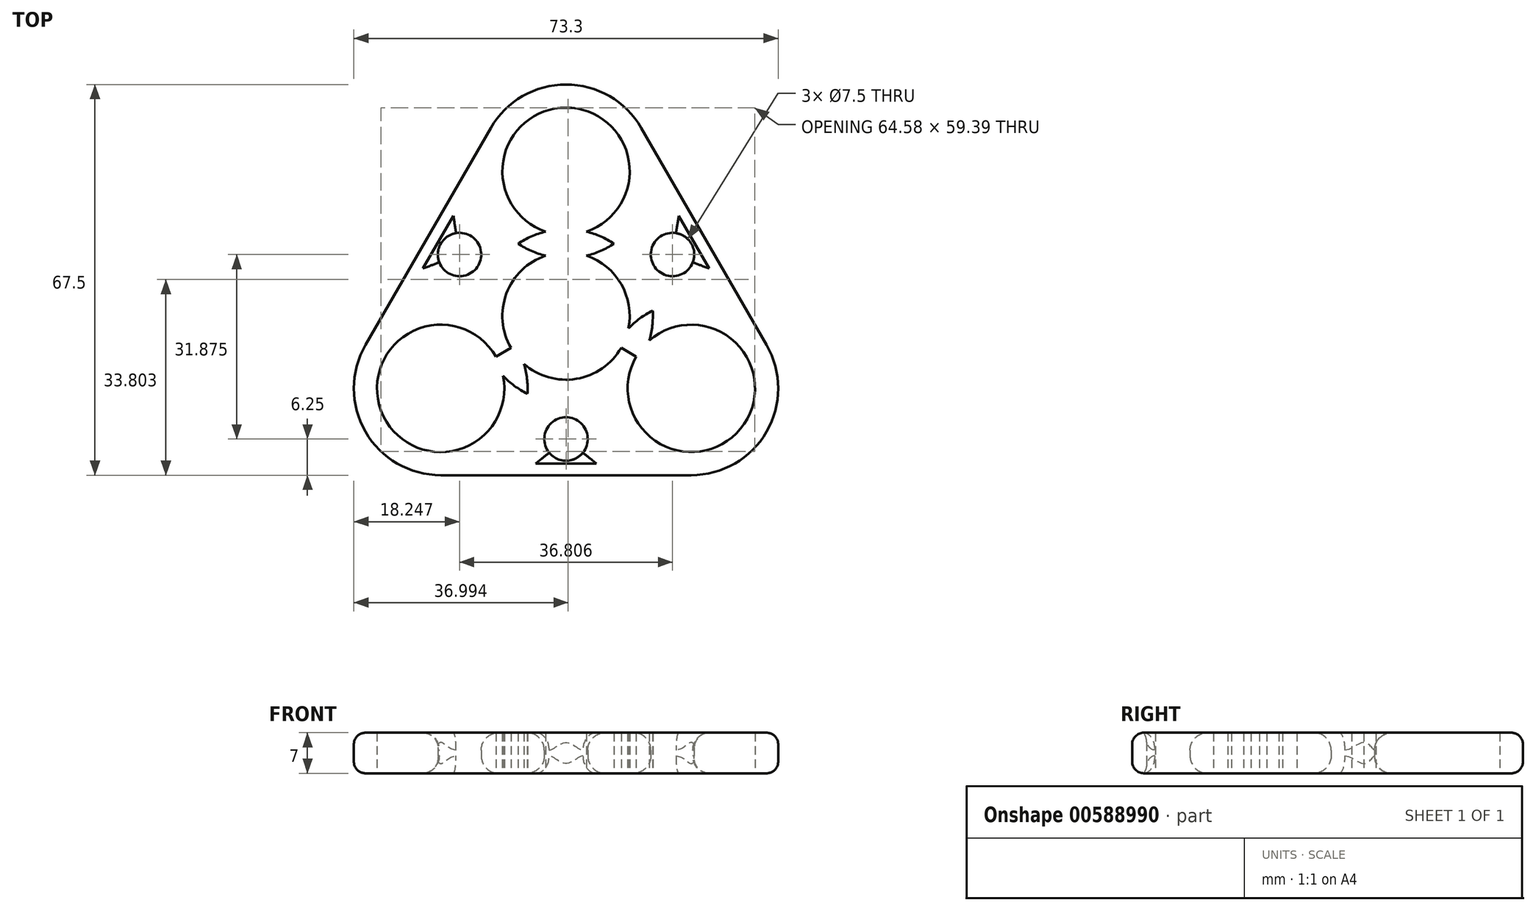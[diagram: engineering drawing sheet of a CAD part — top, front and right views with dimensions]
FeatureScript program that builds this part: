
annotation { "Feature Type Name" : "Feature", "Feature Type Description" : "" }
export const myFeature = defineFeature(function(context is Context, id is Id, definition is map)
    precondition{}
    {
        {
            var Q0;
            Q0=qCreatedBy(makeId("Top.planeOp"),FACE);
            var sketch = newSketch(context, id + "F0", { "sketchPlane" : qUnion([Q0])});
            skCircle(sketch, "E0", {"center": v(0, 0) * mm, "radius": 11 * mm});
            skCircle(sketch, "E1", {"center": v(0, 0) * mm, "radius": 15 * mm});
            skLineSegment(sketch, "E2", {"start": v(0, 0) * mm, "end": v(0, 25) * mm});
            skLineSegment(sketch, "E3", {"start": v(0, 25) * mm, "end": v(0, 0) * mm});
            skLineSegment(sketch, "E4", {"start": v(0, 0) * mm, "end": v(21.65, -12.5) * mm});
            skLineSegment(sketch, "E5", {"start": v(21.65, -12.5) * mm, "end": v(0, 0) * mm});
            skLineSegment(sketch, "E6", {"start": v(0, 0) * mm, "end": v(-21.65, -12.5) * mm});
            skLineSegment(sketch, "E7", {"start": v(-21.65, -12.5) * mm, "end": v(0, 0) * mm});
            skCircle(sketch, "E8", {"center": v(0, 25) * mm, "radius": 11 * mm});
            skCircle(sketch, "E9", {"center": v(21.65, -12.5) * mm, "radius": 11 * mm});
            skCircle(sketch, "E10", {"center": v(21.65, -12.5) * mm, "radius": 15 * mm});
            skCircle(sketch, "E11", {"center": v(0, 25) * mm, "radius": 15 * mm});
            skCircle(sketch, "E12", {"center": v(-21.65, -12.5) * mm, "radius": 11 * mm});
            skCircle(sketch, "E13", {"center": v(-21.65, -12.5) * mm, "radius": 15 * mm});
            skLineSegment(sketch, "E14", {"start": v(-21.65, -12.5) * mm, "end": v(-47.63, -27.5) * mm});
            skLineSegment(sketch, "E15", {"start": v(21.65, -12.5) * mm, "end": v(47.63, -27.5) * mm});
            skLineSegment(sketch, "E16", {"start": v(0, 25) * mm, "end": v(0, 55) * mm});
            skLineSegment(sketch, "E17", {"start": v(-43.3, -20) * mm, "end": v(-4.33, 47.5) * mm});
            skLineSegment(sketch, "E18", {"start": v(43.3, -20) * mm, "end": v(4.33, 47.5) * mm});
            skLineSegment(sketch, "E19", {"start": v(38.97, -27.5) * mm, "end": v(-38.97, -27.5) * mm});
            skPoint(sketch, "E20.visualSharp", {"position": v(-47.63, -27.5) * mm});
            skArc(sketch, "E20.filletArc", {"start": v(-43.3, -20) * mm, "mid": v(-43.3, -25) * mm, "end": v(-38.97, -27.5) * mm});
            skPoint(sketch, "E21.visualSharp", {"position": v(47.63, -27.5) * mm});
            skArc(sketch, "E21.filletArc", {"start": v(38.97, -27.5) * mm, "mid": v(43.3, -25) * mm, "end": v(43.3, -20) * mm});
            skPoint(sketch, "E22.visualSharp", {"position": v(0, 55) * mm});
            skArc(sketch, "E22.filletArc", {"start": v(4.33, 47.5) * mm, "mid": v(0, 50) * mm, "end": v(-4.33, 47.5) * mm});
            skCircle(sketch, "E23", {"center": v(-18.4, 10.62) * mm, "radius": 3.75 * mm});
            skLineSegment(sketch, "E24", {"start": v(0, 0) * mm, "end": v(-25.93, 14.97) * mm});
            skLineSegment(sketch, "E25", {"start": v(0, 0) * mm, "end": v(0, -23.93) * mm});
            skLineSegment(sketch, "E26", {"start": v(0, 0) * mm, "end": v(26.53, 15.32) * mm});
            skCircle(sketch, "E27", {"center": v(18.4, 10.62) * mm, "radius": 3.75 * mm});
            skCircle(sketch, "E28", {"center": v(0, -21.25) * mm, "radius": 3.75 * mm});
            skSolve(sketch);
        }
        {
            var Q0;
            {var subQ0=sQuery(id+"F0.wireOp",EDGE,"E11");var subQ1=sQuery(id+"F0.wireOp",EDGE,"E1");var subQ2=makeQuery(id+"F0.imprint","INTERSECT",VERTEX,{"disambiguationData":[OD(0.0)],"derivedFrom":[subQ1,subQ0]});Q0=makeQuery(id+"F0.imprint","IMPRINT",FACE,{"disambiguationData":[TD([[makeQuery(id+"F0.imprint","IMPRINT",EDGE,{"disambiguationData":[TD([[subQ2,1.0]])],"derivedFrom":subQ1}),-1.0]])]});}
            var Q1;
            {var subQ0=sQuery(id+"F0.wireOp",EDGE,"E11");var subQ1=sQuery(id+"F0.wireOp",EDGE,"E1");var subQ2=makeQuery(id+"F0.imprint","INTERSECT",VERTEX,{"disambiguationData":[OD(1.0)],"derivedFrom":[subQ1,subQ0]});Q1=makeQuery(id+"F0.imprint","IMPRINT",FACE,{"disambiguationData":[TD([[makeQuery(id+"F0.imprint","IMPRINT",EDGE,{"disambiguationData":[TD([[subQ2,-1.0]])],"derivedFrom":subQ1}),-1.0]])]});}
            var Q2;
            {var subQ0=sQuery(id+"F0.wireOp",EDGE,"E13");var subQ1=sQuery(id+"F0.wireOp",EDGE,"E1");var subQ2=makeQuery(id+"F0.imprint","INTERSECT",VERTEX,{"disambiguationData":[OD(1.0)],"derivedFrom":[subQ1,subQ0]});Q2=makeQuery(id+"F0.imprint","IMPRINT",FACE,{"disambiguationData":[TD([[makeQuery(id+"F0.imprint","IMPRINT",EDGE,{"disambiguationData":[TD([[subQ2,-1.0]])],"derivedFrom":subQ1}),-1.0]])]});}
            var Q3;
            {var subQ0=sQuery(id+"F0.wireOp",EDGE,"E11");var subQ2=sQuery(id+"F0.wireOp",EDGE,"E1");var subQ3=makeQuery(id+"F0.imprint","INTERSECT",VERTEX,{"disambiguationData":[OD(0.0)],"derivedFrom":[subQ2,subQ0]});Q3=makeQuery(id+"F0.imprint","IMPRINT",FACE,{"disambiguationData":[TD([[makeQuery(id+"F0.imprint","IMPRINT",EDGE,{"disambiguationData":[TD([[subQ3,-1.0]])],"derivedFrom":subQ2}),-1.0]])]});}
            var Q4;
            {var subQ2=sQuery(id+"F0.wireOp",EDGE,"E1");var subQ4=sQuery(id+"F0.wireOp",EDGE,"E8");var subQ5=makeQuery(id+"F0.imprint","INTERSECT",VERTEX,{"disambiguationData":[OD(1.0)],"derivedFrom":[subQ2,subQ4]});Q4=makeQuery(id+"F0.imprint","IMPRINT",FACE,{"disambiguationData":[TD([[makeQuery(id+"F0.imprint","IMPRINT",EDGE,{"disambiguationData":[TD([[subQ5,-1.0]])],"derivedFrom":subQ2}),-1.0]])]});}
            var Q5;
            {var subQ0=sQuery(id+"F0.wireOp",EDGE,"E13");var subQ4=sQuery(id+"F0.wireOp",EDGE,"E1");var subQ5=makeQuery(id+"F0.imprint","INTERSECT",VERTEX,{"disambiguationData":[OD(0.0)],"derivedFrom":[subQ4,subQ0]});Q5=makeQuery(id+"F0.imprint","IMPRINT",FACE,{"disambiguationData":[TD([[makeQuery(id+"F0.imprint","IMPRINT",EDGE,{"disambiguationData":[TD([[subQ5,-1.0]])],"derivedFrom":subQ4}),-1.0]])]});}
            var Q6;
            {var subQ4=sQuery(id+"F0.wireOp",EDGE,"E12");var subQ5=sQuery(id+"F0.wireOp",EDGE,"E1");var subQ6=makeQuery(id+"F0.imprint","INTERSECT",VERTEX,{"disambiguationData":[OD(1.0)],"derivedFrom":[subQ5,subQ4]});Q6=makeQuery(id+"F0.imprint","IMPRINT",FACE,{"disambiguationData":[TD([[makeQuery(id+"F0.imprint","IMPRINT",EDGE,{"disambiguationData":[TD([[subQ6,-1.0]])],"derivedFrom":subQ5}),-1.0]])]});}
            var Q7;
            {var subQ0=sQuery(id+"F0.wireOp",EDGE,"E10");var subQ4=sQuery(id+"F0.wireOp",EDGE,"E1");var subQ5=makeQuery(id+"F0.imprint","INTERSECT",VERTEX,{"disambiguationData":[OD(1.0)],"derivedFrom":[subQ4,subQ0]});Q7=makeQuery(id+"F0.imprint","IMPRINT",FACE,{"disambiguationData":[TD([[makeQuery(id+"F0.imprint","IMPRINT",EDGE,{"disambiguationData":[TD([[subQ5,-1.0]])],"derivedFrom":subQ4}),-1.0]])]});}
            var Q8;
            {var subQ0=sQuery(id+"F0.wireOp",EDGE,"E10");var subQ4=sQuery(id+"F0.wireOp",EDGE,"E1");var subQ5=makeQuery(id+"F0.imprint","INTERSECT",VERTEX,{"disambiguationData":[OD(0.0)],"derivedFrom":[subQ4,subQ0]});Q8=makeQuery(id+"F0.imprint","IMPRINT",FACE,{"disambiguationData":[TD([[makeQuery(id+"F0.imprint","IMPRINT",EDGE,{"disambiguationData":[TD([[subQ5,1.0]])],"derivedFrom":subQ4}),-1.0]])]});}
            var Q9;
            {var subQ0=sQuery(id+"F0.wireOp",EDGE,"E11");var subQ1=sQuery(id+"F0.wireOp",EDGE,"E0");var subQ2=makeQuery(id+"F0.imprint","INTERSECT",VERTEX,{"disambiguationData":[OD(1.0)],"derivedFrom":[subQ1,subQ0]});Q9=makeQuery(id+"F0.imprint","IMPRINT",FACE,{"disambiguationData":[TD([[makeQuery(id+"F0.imprint","IMPRINT",EDGE,{"disambiguationData":[TD([[subQ2,-1.0]])],"derivedFrom":subQ1}),-1.0]])]});}
            var Q10;
            {var subQ5=sQuery(id+"F0.wireOp",EDGE,"E0");var subQ7=sQuery(id+"F0.wireOp",EDGE,"E13");var subQ8=makeQuery(id+"F0.imprint","INTERSECT",VERTEX,{"disambiguationData":[OD(0.0)],"derivedFrom":[subQ5,subQ7]});Q10=makeQuery(id+"F0.imprint","IMPRINT",FACE,{"disambiguationData":[TD([[makeQuery(id+"F0.imprint","IMPRINT",EDGE,{"disambiguationData":[TD([[subQ8,-1.0]])],"derivedFrom":subQ5}),-1.0]])]});}
            var Q11;
            {var subQ0=sQuery(id+"F0.wireOp",EDGE,"E7");var subQ1=sQuery(id+"F0.wireOp",EDGE,"E0");var subQ2=makeQuery(id+"F0.imprint","INTERSECT",VERTEX,{"derivedFrom":[subQ1,subQ0]});Q11=makeQuery(id+"F0.imprint","IMPRINT",FACE,{"disambiguationData":[TD([[makeQuery(id+"F0.imprint","IMPRINT",EDGE,{"disambiguationData":[TD([[subQ2,-1.0]])],"derivedFrom":subQ1}),-1.0]])]});}
            var Q12;
            {var subQ0=sQuery(id+"F0.wireOp",EDGE,"E13");var subQ1=sQuery(id+"F0.wireOp",EDGE,"E0");var subQ2=makeQuery(id+"F0.imprint","INTERSECT",VERTEX,{"disambiguationData":[OD(1.0)],"derivedFrom":[subQ1,subQ0]});Q12=makeQuery(id+"F0.imprint","IMPRINT",FACE,{"disambiguationData":[TD([[makeQuery(id+"F0.imprint","IMPRINT",EDGE,{"disambiguationData":[TD([[subQ2,-1.0]])],"derivedFrom":subQ1}),-1.0]])]});}
            var Q13;
            {var subQ5=sQuery(id+"F0.wireOp",EDGE,"E10");var subQ7=sQuery(id+"F0.wireOp",EDGE,"E0");var subQ9=makeQuery(id+"F0.imprint","INTERSECT",VERTEX,{"disambiguationData":[OD(0.0)],"derivedFrom":[subQ7,subQ5]});Q13=makeQuery(id+"F0.imprint","IMPRINT",FACE,{"disambiguationData":[TD([[makeQuery(id+"F0.imprint","IMPRINT",EDGE,{"disambiguationData":[TD([[subQ9,-1.0]])],"derivedFrom":subQ7}),-1.0]])]});}
            var Q14;
            {var subQ0=sQuery(id+"F0.wireOp",EDGE,"E5");var subQ1=sQuery(id+"F0.wireOp",EDGE,"E0");var subQ2=makeQuery(id+"F0.imprint","INTERSECT",VERTEX,{"derivedFrom":[subQ1,subQ0]});Q14=makeQuery(id+"F0.imprint","IMPRINT",FACE,{"disambiguationData":[TD([[makeQuery(id+"F0.imprint","IMPRINT",EDGE,{"disambiguationData":[TD([[subQ2,-1.0]])],"derivedFrom":subQ1}),-1.0]])]});}
            var Q15;
            {var subQ0=sQuery(id+"F0.wireOp",EDGE,"E11");var subQ1=sQuery(id+"F0.wireOp",EDGE,"E0");var subQ2=makeQuery(id+"F0.imprint","INTERSECT",VERTEX,{"disambiguationData":[OD(0.0)],"derivedFrom":[subQ1,subQ0]});Q15=makeQuery(id+"F0.imprint","IMPRINT",FACE,{"disambiguationData":[TD([[makeQuery(id+"F0.imprint","IMPRINT",EDGE,{"disambiguationData":[TD([[subQ2,1.0]])],"derivedFrom":subQ1}),-1.0]])]});}
            var Q16;
            {var subQ3=sQuery(id+"F0.wireOp",EDGE,"E3");var subQ5=sQuery(id+"F0.wireOp",EDGE,"E0");var subQ6=makeQuery(id+"F0.imprint","INTERSECT",VERTEX,{"derivedFrom":[subQ5,subQ3]});Q16=makeQuery(id+"F0.imprint","IMPRINT",FACE,{"disambiguationData":[TD([[makeQuery(id+"F0.imprint","IMPRINT",EDGE,{"disambiguationData":[TD([[subQ6,1.0]])],"derivedFrom":subQ5}),-1.0]])]});}
            var Q17;
            {var subQ3=sQuery(id+"F0.wireOp",EDGE,"E3");var subQ7=sQuery(id+"F0.wireOp",EDGE,"E0");var subQ8=makeQuery(id+"F0.imprint","INTERSECT",VERTEX,{"derivedFrom":[subQ7,subQ3]});Q17=makeQuery(id+"F0.imprint","IMPRINT",FACE,{"disambiguationData":[TD([[makeQuery(id+"F0.imprint","IMPRINT",EDGE,{"disambiguationData":[TD([[subQ8,-1.0]])],"derivedFrom":subQ7}),-1.0]])]});}
            var Q18;
            {var subQ0=sQuery(id+"F0.wireOp",EDGE,"E24");var subQ4=sQuery(id+"F0.wireOp",EDGE,"E1");var subQ5=makeQuery(id+"F0.imprint","INTERSECT",VERTEX,{"derivedFrom":[subQ4,subQ0]});Q18=makeQuery(id+"F0.imprint","IMPRINT",FACE,{"disambiguationData":[TD([[makeQuery(id+"F0.imprint","IMPRINT",EDGE,{"disambiguationData":[TD([[subQ5,-1.0]])],"derivedFrom":subQ4}),-1.0]])]});}
            var Q19;
            {var subQ0=sQuery(id+"F0.wireOp",EDGE,"E24");var subQ1=sQuery(id+"F0.wireOp",EDGE,"E0");var subQ2=makeQuery(id+"F0.imprint","INTERSECT",VERTEX,{"derivedFrom":[subQ1,subQ0]});Q19=makeQuery(id+"F0.imprint","IMPRINT",FACE,{"disambiguationData":[TD([[makeQuery(id+"F0.imprint","IMPRINT",EDGE,{"disambiguationData":[TD([[subQ2,-1.0]])],"derivedFrom":subQ1}),-1.0]])]});}
            var Q20;
            {var subQ0=sQuery(id+"F0.wireOp",EDGE,"E26");var subQ1=sQuery(id+"F0.wireOp",EDGE,"E0");var subQ2=makeQuery(id+"F0.imprint","INTERSECT",VERTEX,{"derivedFrom":[subQ1,subQ0]});Q20=makeQuery(id+"F0.imprint","IMPRINT",FACE,{"disambiguationData":[TD([[makeQuery(id+"F0.imprint","IMPRINT",EDGE,{"disambiguationData":[TD([[subQ2,1.0]])],"derivedFrom":subQ1}),-1.0]])]});}
            var Q21;
            {var subQ0=sQuery(id+"F0.wireOp",EDGE,"E26");var subQ5=sQuery(id+"F0.wireOp",EDGE,"E1");var subQ6=makeQuery(id+"F0.imprint","INTERSECT",VERTEX,{"derivedFrom":[subQ5,subQ0]});Q21=makeQuery(id+"F0.imprint","IMPRINT",FACE,{"disambiguationData":[TD([[makeQuery(id+"F0.imprint","IMPRINT",EDGE,{"disambiguationData":[TD([[subQ6,1.0]])],"derivedFrom":subQ5}),-1.0]])]});}
            var Q22;
            {var subQ0=sQuery(id+"F0.wireOp",EDGE,"E25");var subQ1=sQuery(id+"F0.wireOp",EDGE,"E0");var subQ2=makeQuery(id+"F0.imprint","INTERSECT",VERTEX,{"derivedFrom":[subQ1,subQ0]});Q22=makeQuery(id+"F0.imprint","IMPRINT",FACE,{"disambiguationData":[TD([[makeQuery(id+"F0.imprint","IMPRINT",EDGE,{"disambiguationData":[TD([[subQ2,-1.0]])],"derivedFrom":subQ1}),-1.0]])]});}
            extrude(context, id + "F1", {"entities" : qUnion([Q0, Q1, Q2, Q3, Q4, Q5, Q6, Q7, Q8, Q9, Q10, Q11, Q12, Q13, Q14, Q15, Q16, Q17, Q18, Q19, Q20, Q21, Q22]), "depth" : 7 * mm, "offsetDistance" : 25 * mm});
        }
        {
            var Q0;
            Q0=makeQuery(id+"F1.opExtrude","CAP_EDGE",EDGE,{"disambiguationData":[OSD([sQuery(id+"F0.wireOp",EDGE,"E19")])],"isStart":false});
            var Q1;
            Q1=makeQuery(id+"F1.opExtrude","CAP_EDGE",EDGE,{"disambiguationData":[OSD([sQuery(id+"F0.wireOp",EDGE,"E19")])],"isStart":true});
            fillet(context, id + "F2", {"entities" : qUnion([Q0, Q1]), "radius" : 2 * mm, "tangentPropagation" : true, "allowEdgeOverflow" : false});
        }
        {
            var Q0;
            Q0=makeQuery(id+"F1.opExtrude","CAP_EDGE",EDGE,{"disambiguationData":[OSD([sQuery(id+"F0.wireOp",EDGE,"E28")])],"isStart":false});
            var Q1;
            Q1=makeQuery(id+"F1.opExtrude","CAP_EDGE",EDGE,{"disambiguationData":[OSD([sQuery(id+"F0.wireOp",EDGE,"E23")])],"isStart":false});
            var Q2;
            Q2=makeQuery(id+"F1.opExtrude","CAP_EDGE",EDGE,{"disambiguationData":[OSD([sQuery(id+"F0.wireOp",EDGE,"E27")])],"isStart":false});
            var Q3;
            Q3=makeQuery(id+"F1.opExtrude","CAP_EDGE",EDGE,{"disambiguationData":[OSD([sQuery(id+"F0.wireOp",EDGE,"E23")])],"isStart":true});
            var Q4;
            Q4=makeQuery(id+"F1.opExtrude","CAP_EDGE",EDGE,{"disambiguationData":[OSD([sQuery(id+"F0.wireOp",EDGE,"E28")])],"isStart":true});
            var Q5;
            Q5=makeQuery(id+"F1.opExtrude","CAP_EDGE",EDGE,{"disambiguationData":[OSD([sQuery(id+"F0.wireOp",EDGE,"E27")])],"isStart":true});
            fillet(context, id + "F3", {"entities" : qUnion([Q0, Q1, Q2, Q3, Q4, Q5]), "radius" : 3 * mm, "tangentPropagation" : true, "allowEdgeOverflow" : false});
        }
    });
